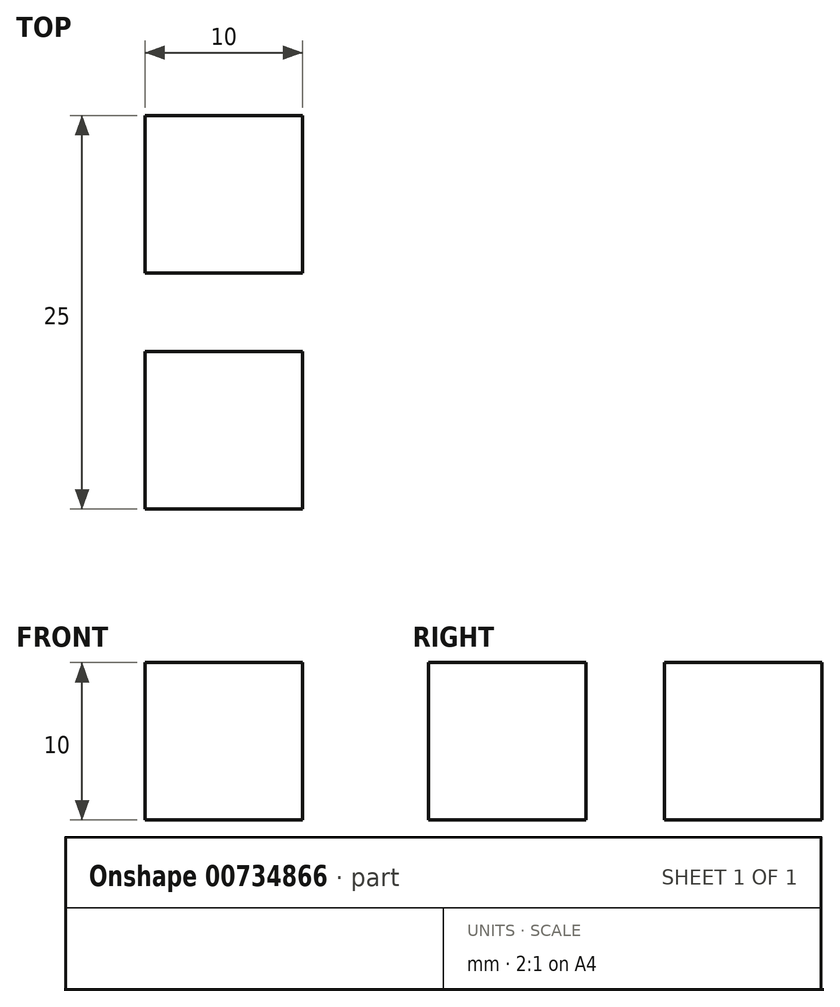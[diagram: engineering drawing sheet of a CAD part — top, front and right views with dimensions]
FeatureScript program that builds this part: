
annotation { "Feature Type Name" : "Feature", "Feature Type Description" : "" }
export const myFeature = defineFeature(function(context is Context, id is Id, definition is map)
    precondition{}
    {
        {
            var Q0;
            Q0=qCreatedBy(makeId("Right.planeOp"),FACE);
            var sketch = newSketch(context, id + "F0", { "sketchPlane" : qUnion([Q0])});
            skLineSegment(sketch, "E0.bottom", {"start": v(0, 0) * mm, "end": v(10, 0) * mm});
            skLineSegment(sketch, "E0.top", {"start": v(0, 10) * mm, "end": v(10, 10) * mm});
            skLineSegment(sketch, "E0.left", {"start": v(0, 0) * mm, "end": v(0, 10) * mm});
            skLineSegment(sketch, "E0.right", {"start": v(10, 0) * mm, "end": v(10, 10) * mm});
            skLineSegment(sketch, "E1.0", {"start": v(15, 0) * mm, "end": v(15, 10) * mm});
            skLineSegment(sketch, "E2.0", {"start": v(25, 0) * mm, "end": v(25, 10) * mm});
            skLineSegment(sketch, "E3", {"start": v(15, 0) * mm, "end": v(25, 0) * mm});
            skLineSegment(sketch, "E4", {"start": v(25, 10) * mm, "end": v(15, 10) * mm});
            skSolve(sketch);
        }
        {
            var Q0;
            Q0=makeQuery(id+"F0.imprint","IMPRINT",FACE,{"disambiguationData":[TD([[makeQuery(id+"F0.imprint","IMPRINT",EDGE,{"derivedFrom":sQuery(id+"F0.wireOp",EDGE,"E0.bottom")}),1.0]])]});
            var Q1;
            Q1=makeQuery(id+"F0.imprint","IMPRINT",FACE,{"disambiguationData":[TD([[makeQuery(id+"F0.imprint","IMPRINT",EDGE,{"derivedFrom":sQuery(id+"F0.wireOp",EDGE,"E1.0")}),-1.0]])]});
            extrude(context, id + "F1", {"entities" : qUnion([Q0, Q1]), "depth" : 10 * mm, "offsetDistance" : 25 * mm});
        }
    });
